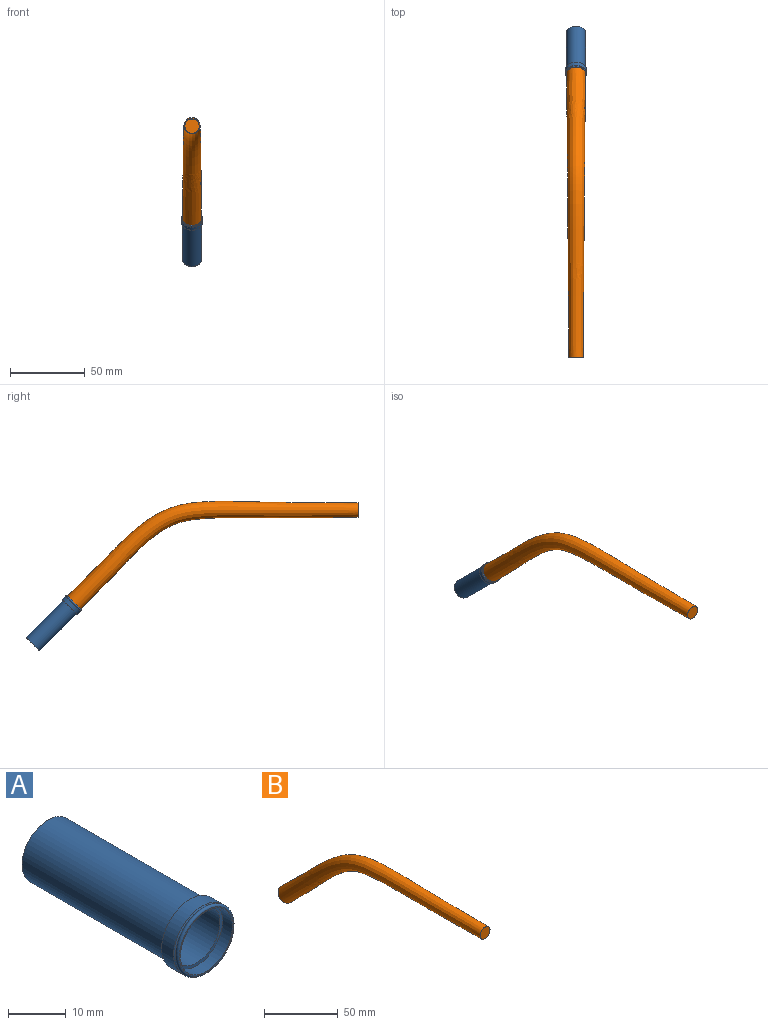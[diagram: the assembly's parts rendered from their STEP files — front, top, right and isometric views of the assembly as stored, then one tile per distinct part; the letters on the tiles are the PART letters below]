
ASSEMBLY  parts=2 mates=1
PART A: 10 faces, bbox 15.2x38.9x15.2 mm
  f0: cylinder r=7.01mm len=14.02mm, axis (0,-1,0), area 129.8mm2, adj f6,f9
  f1: plane 13.23x13.23mm, normal (0,-1,0), area 9.7mm2, adj f7,f8
  f2: plane 12.75x12.75mm, normal (0,-1,0), area 25.1mm2, adj f3,f7
  f3: cylinder r=5.71mm len=36.51mm, axis (0,-1,0), area 1311.1mm2, adj f2,f4
  f4: plane 12.7x12.7mm, normal (0,1,0), area 24.1mm2, adj f3,f5
  f5: cylinder r=6.35mm len=34.93mm, axis (0,-1,0), area 1393.4mm2, adj f4,f6
  f6: plane 14.02x14.02mm, normal (0,1,0), area 27.7mm2, adj f0,f5
  f7: cylinder r=6.38mm len=12.75mm, axis (0,-1,0), area 95.4mm2, adj f1,f2
  f8: torus R=6.61mm, axis (0,-1,0), area 53.8mm2, adj f1,f9
  f9: cone r=6.61mm half-angle=60deg, axis (0,1,0), area 19.6mm2, adj f0,f8
PART B: 3 faces, bbox 12.7x195.9x73.8 mm
  f0: plane 12.7x8.98mm, normal (0,0.71,-0.71), area 126.7mm2, adj f2
  f1: plane 9.53x9.53mm, normal (0,-1,0), area 71.3mm2, adj f2
  f2: bspline ~195.89x73.82mm, area 7503.1mm2, adj f0,f1
PLACE A rot(axis=(-1,0,0),45deg) t=(0,-1.68,1.68)mm
PLACE B at identity
MATE fastened A.f0 <-> B.f0  axis (0,-0.71,0.71) through (0,0,0)mm
